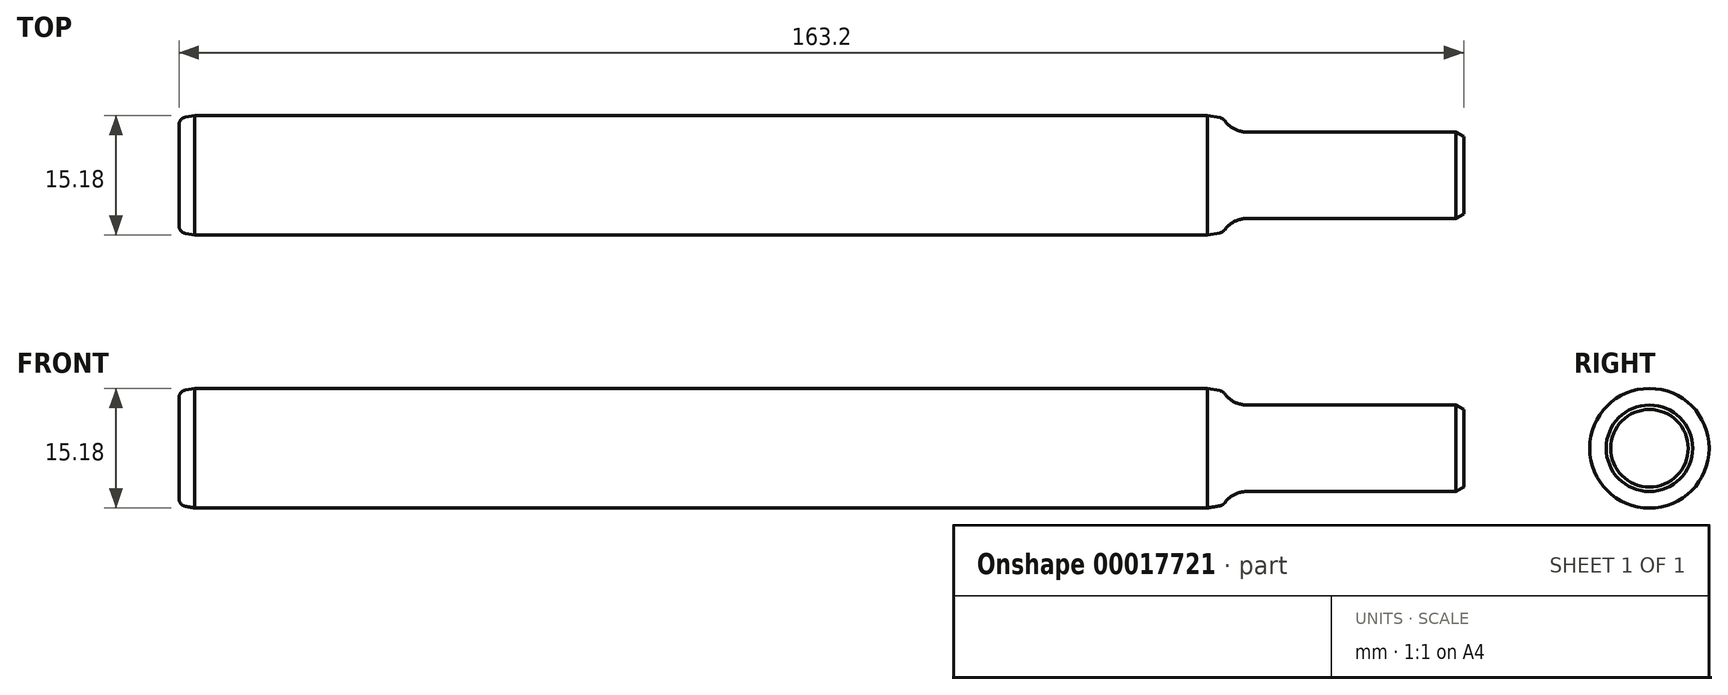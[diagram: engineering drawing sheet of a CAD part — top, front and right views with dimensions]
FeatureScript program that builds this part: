
annotation { "Feature Type Name" : "Feature", "Feature Type Description" : "" }
export const myFeature = defineFeature(function(context is Context, id is Id, definition is map)
    precondition{}
    {
        {
            var Q0;
            Q0=qCreatedBy(makeId("Front.planeOp"),FACE);
            var sketch = newSketch(context, id + "F0", { "sketchPlane" : qUnion([Q0])});
            skLineSegment(sketch, "E0", {"start": v(0, 0) * mm, "end": v(0, 6.4) * mm});
            skLineSegment(sketch, "E1", {"start": v(2, 7.6) * mm, "end": v(130.62, 7.6) * mm});
            skLineSegment(sketch, "E2", {"start": v(130.62, 7.6) * mm, "end": v(132.2, 7.31) * mm});
            skLineSegment(sketch, "E3", {"start": v(135.66, 5.5) * mm, "end": v(162.2, 5.5) * mm});
            skLineSegment(sketch, "E4", {"start": v(163.2, 4.92) * mm, "end": v(163.2, 0) * mm});
            skLineSegment(sketch, "E5", {"start": v(163.2, 0) * mm, "end": v(0, 0) * mm});
            skArc(sketch, "E6", {"start": v(132.83, 6.93) * mm, "mid": v(134.08, 5.87) * mm, "end": v(135.66, 5.5) * mm});
            skPoint(sketch, "E7.visualSharp", {"position": v(132.63, 7.24) * mm});
            skArc(sketch, "E7.filletArc", {"start": v(132.83, 6.93) * mm, "mid": v(132.56, 7.18) * mm, "end": v(132.2, 7.31) * mm});
            skLineSegment(sketch, "E8", {"start": v(2, 7.6) * mm, "end": v(0.82, 7.39) * mm});
            skPoint(sketch, "E9.orphan", {"position": v(0, 7.6) * mm});
            skPoint(sketch, "E10.visualSharp", {"position": v(0, 7.24) * mm});
            skArc(sketch, "E10.filletArc", {"start": v(0.82, 7.39) * mm, "mid": v(0.23, 7.05) * mm, "end": v(0, 6.4) * mm});
            skLineSegment(sketch, "E11", {"start": v(162.2, 5.5) * mm, "end": v(163.2, 4.92) * mm});
            skSolve(sketch);
        }
        {
            var Q0;
            Q0=makeQuery(id+"F0.imprint","IMPRINT",FACE,{"disambiguationData":[TD([[makeQuery(id+"F0.imprint","IMPRINT",EDGE,{"derivedFrom":sQuery(id+"F0.wireOp",EDGE,"E0")}),-1.0]])]});
            var Q1;
            Q1=sQuery(id+"F0.wireOp",EDGE,"E5");
            revolve(context, id + "F1", {"entities" : qUnion([Q0]), "axis" : qUnion([Q1]), "revolveType" : RevolveType.FULL});
        }
    });
